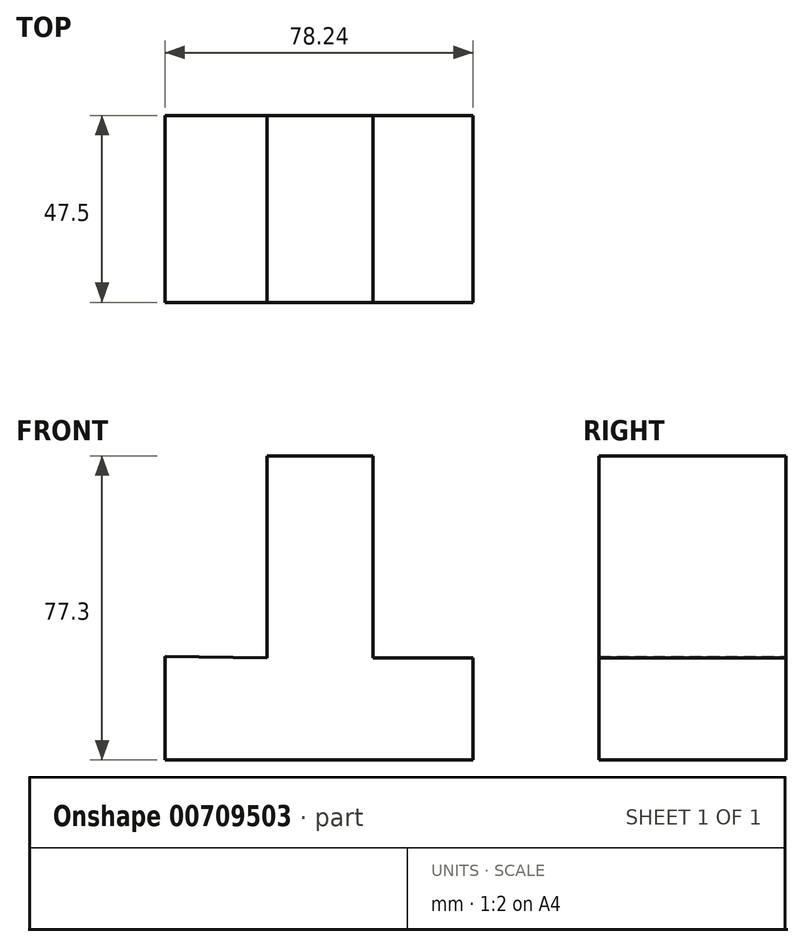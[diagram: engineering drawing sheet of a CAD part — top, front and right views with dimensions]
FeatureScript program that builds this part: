
annotation { "Feature Type Name" : "Feature", "Feature Type Description" : "" }
export const myFeature = defineFeature(function(context is Context, id is Id, definition is map)
    precondition{}
    {
        {
            var Q0;
            Q0=qCreatedBy(makeId("Front.planeOp"),FACE);
            var sketch = newSketch(context, id + "F0", { "sketchPlane" : qUnion([Q0])});
            skLineSegment(sketch, "E0", {"start": v(-56.91, 18.62) * mm, "end": v(-56.91, -7.78) * mm});
            skLineSegment(sketch, "E1", {"start": v(-56.91, -7.78) * mm, "end": v(21.33, -7.78) * mm});
            skLineSegment(sketch, "E2", {"start": v(21.33, -7.78) * mm, "end": v(21.33, 18.15) * mm});
            skLineSegment(sketch, "E3", {"start": v(21.33, 18.15) * mm, "end": v(-4.12, 18.15) * mm});
            skLineSegment(sketch, "E4", {"start": v(-4.12, 18.15) * mm, "end": v(-4.12, 69.52) * mm});
            skLineSegment(sketch, "E5", {"start": v(-4.12, 69.52) * mm, "end": v(-31, 69.52) * mm});
            skLineSegment(sketch, "E6", {"start": v(-31, 69.52) * mm, "end": v(-31, 18.15) * mm});
            skLineSegment(sketch, "E7", {"start": v(-31, 18.15) * mm, "end": v(-56.91, 18.62) * mm});
            skSolve(sketch);
        }
        {
            var Q0;
            Q0 = qSketchRegion(id + "F0", true);
            extrude(context, id + "F1", {"entities" : qUnion([Q0]), "depth" : 47.5 * mm, "offsetDistance" : 25.4 * mm});
        }
    });
